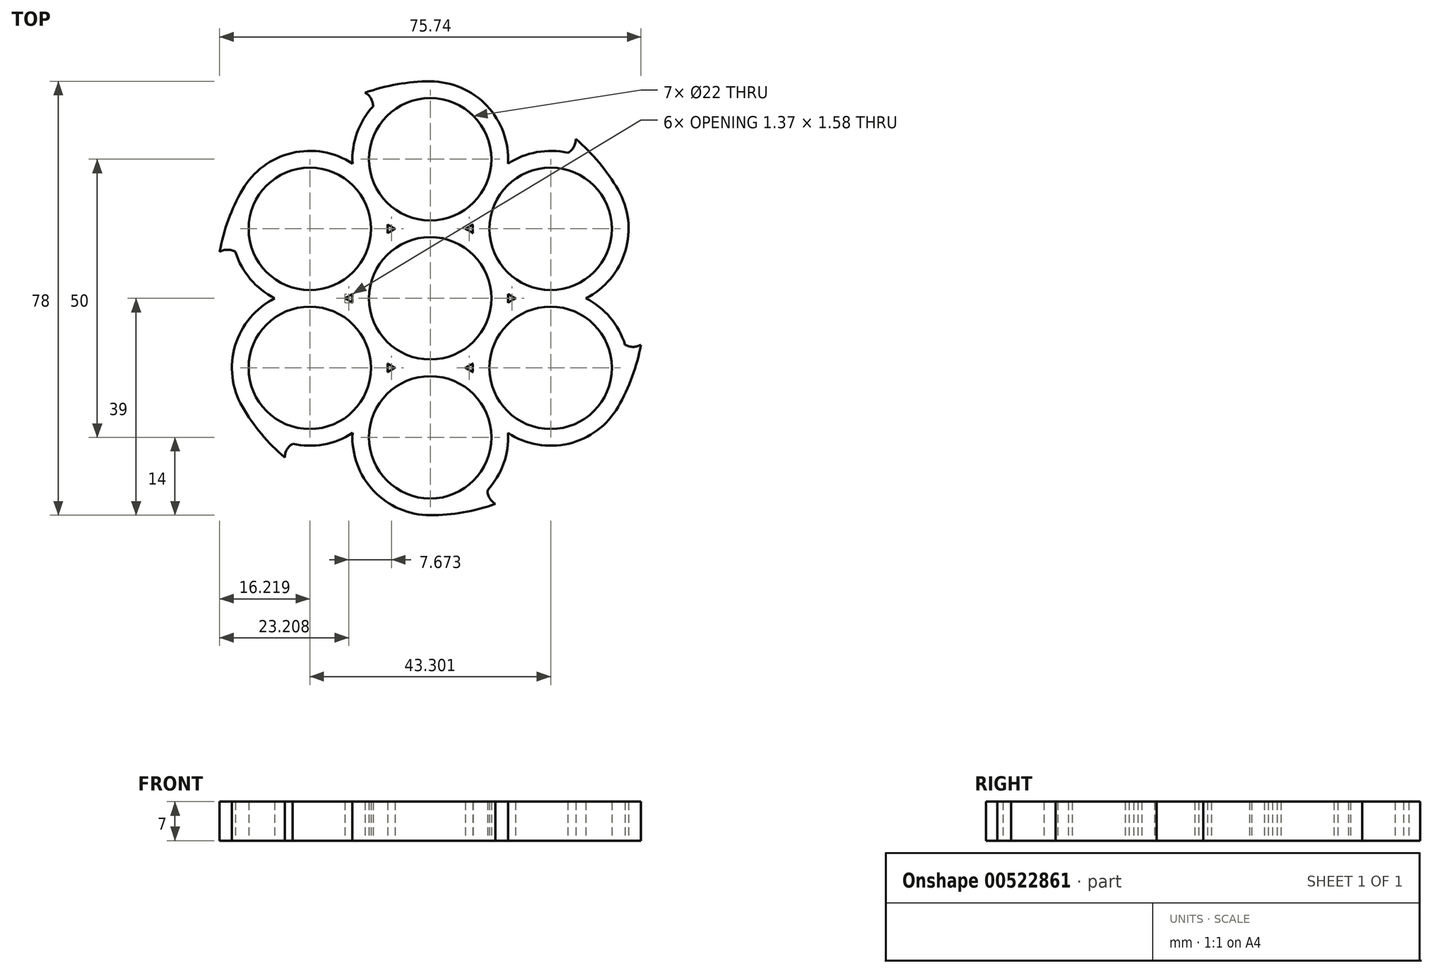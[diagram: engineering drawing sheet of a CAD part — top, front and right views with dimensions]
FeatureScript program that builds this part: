
annotation { "Feature Type Name" : "Feature", "Feature Type Description" : "" }
export const myFeature = defineFeature(function(context is Context, id is Id, definition is map)
    precondition{}
    {
        {
            var Q0;
            Q0=qCreatedBy(makeId("Top.planeOp"),FACE);
            var sketch = newSketch(context, id + "F0", { "sketchPlane" : qUnion([Q0])});
            skCircle(sketch, "E0", {"center": v(0, 0) * mm, "radius": 11 * mm});
            skArc(sketch, "E1", {"start": v(-13.98, 0.79) * mm, "mid": v(-14, 0) * mm, "end": v(-13.98, -0.79) * mm});
            skCircle(sketch, "E2", {"center": v(0, 25) * mm, "radius": 11 * mm});
            skArc(sketch, "E3", {"start": v(-7.67, 13.29) * mm, "mid": v(-7, 12.88) * mm, "end": v(-6.3, 12.5) * mm});
            skCircle(sketch, "E4.1.0", {"center": v(-21.65, 12.5) * mm, "radius": 11 * mm});
            skArc(sketch, "E4.1.1", {"start": v(-7.67, 11.71) * mm, "mid": v(-7.65, 12.5) * mm, "end": v(-7.67, 13.29) * mm});
            skCircle(sketch, "E4.2.0", {"center": v(-21.65, -12.5) * mm, "radius": 11 * mm});
            skArc(sketch, "E4.2.1", {"start": v(-7.67, -13.29) * mm, "mid": v(-7.65, -12.5) * mm, "end": v(-7.67, -11.71) * mm});
            skCircle(sketch, "E4.3.0", {"center": v(0, -25) * mm, "radius": 11 * mm});
            skArc(sketch, "E4.3.1", {"start": v(7.67, -13.29) * mm, "mid": v(7, -12.88) * mm, "end": v(6.3, -12.5) * mm});
            skCircle(sketch, "E4.4.0", {"center": v(21.65, -12.5) * mm, "radius": 11 * mm});
            skArc(sketch, "E4.4.1", {"start": v(7.67, -11.71) * mm, "mid": v(7.65, -12.5) * mm, "end": v(7.67, -13.29) * mm});
            skCircle(sketch, "E4.5.0", {"center": v(21.65, 12.5) * mm, "radius": 11 * mm});
            skArc(sketch, "E4.5.1", {"start": v(7.67, 13.29) * mm, "mid": v(7.65, 12.5) * mm, "end": v(7.67, 11.71) * mm});
            skArc(sketch, "E5.trimOffspring", {"start": v(-13.98, 24.21) * mm, "mid": v(-33.77, 19.5) * mm, "end": v(-27.96, 0) * mm});
            skArc(sketch, "E6.trimOffspring", {"start": v(-6.3, 12.5) * mm, "mid": v(-7, 12.12) * mm, "end": v(-7.67, 11.71) * mm});
            skArc(sketch, "E7.trimOffspring", {"start": v(6.3, 12.5) * mm, "mid": v(7, 12.88) * mm, "end": v(7.67, 13.29) * mm});
            skArc(sketch, "E8.trimOffspring", {"start": v(7.67, 11.71) * mm, "mid": v(7, 12.12) * mm, "end": v(6.3, 12.5) * mm});
            skArc(sketch, "E9.trimOffspring", {"start": v(13.98, 24.21) * mm, "mid": v(0, 39) * mm, "end": v(-13.98, 24.21) * mm});
            skArc(sketch, "E10.trimOffspring", {"start": v(13.98, 0.79) * mm, "mid": v(14.65, 0.38) * mm, "end": v(15.35, 0) * mm});
            skArc(sketch, "E11.trimOffspring", {"start": v(13.98, -0.79) * mm, "mid": v(14, 0) * mm, "end": v(13.98, 0.79) * mm});
            skArc(sketch, "E12.trimOffspring", {"start": v(27.96, 0) * mm, "mid": v(33.77, 19.5) * mm, "end": v(13.98, 24.21) * mm});
            skArc(sketch, "E13.trimOffspring", {"start": v(15.35, 0) * mm, "mid": v(14.65, -0.38) * mm, "end": v(13.98, -0.79) * mm});
            skArc(sketch, "E14.trimOffspring", {"start": v(13.98, -24.21) * mm, "mid": v(33.77, -19.5) * mm, "end": v(27.96, 0) * mm});
            skArc(sketch, "E15.trimOffspring", {"start": v(-6.3, -12.5) * mm, "mid": v(-7, -12.88) * mm, "end": v(-7.67, -13.29) * mm});
            skArc(sketch, "E16.trimOffspring", {"start": v(6.3, -12.5) * mm, "mid": v(7, -12.12) * mm, "end": v(7.67, -11.71) * mm});
            skArc(sketch, "E17.trimOffspring", {"start": v(-13.98, -24.21) * mm, "mid": v(0, -39) * mm, "end": v(13.98, -24.21) * mm});
            skArc(sketch, "E18.trimOffspring", {"start": v(-13.98, -0.79) * mm, "mid": v(-14.65, -0.38) * mm, "end": v(-15.35, 0) * mm});
            skArc(sketch, "E19.trimOffspring", {"start": v(-7.67, -11.71) * mm, "mid": v(-7, -12.12) * mm, "end": v(-6.3, -12.5) * mm});
            skArc(sketch, "E20.trimOffspring", {"start": v(-15.35, 0) * mm, "mid": v(-14.65, 0.38) * mm, "end": v(-13.98, 0.79) * mm});
            skArc(sketch, "E21.trimOffspring", {"start": v(-27.96, 0) * mm, "mid": v(-33.77, -19.5) * mm, "end": v(-13.98, -24.21) * mm});
            skArc(sketch, "E22", {"start": v(0, 39) * mm, "mid": v(-5.94, 38.49) * mm, "end": v(-11.7, 36.97) * mm});
            skArc(sketch, "E23", {"start": v(-10.28, 34.5) * mm, "mid": v(-10.66, 35.93) * mm, "end": v(-11.7, 36.97) * mm});
            skArc(sketch, "E24.1.0", {"start": v(-33.77, 19.5) * mm, "mid": v(-36.3, 14.1) * mm, "end": v(-37.87, 8.34) * mm});
            skArc(sketch, "E24.1.1", {"start": v(-35.02, 8.35) * mm, "mid": v(-36.45, 8.73) * mm, "end": v(-37.87, 8.34) * mm});
            skArc(sketch, "E24.2.0", {"start": v(-33.77, -19.5) * mm, "mid": v(-30.36, -24.4) * mm, "end": v(-26.16, -28.62) * mm});
            skArc(sketch, "E24.2.1", {"start": v(-24.74, -26.16) * mm, "mid": v(-25.79, -27.2) * mm, "end": v(-26.16, -28.62) * mm});
            skArc(sketch, "E24.3.0", {"start": v(0, -39) * mm, "mid": v(5.94, -38.49) * mm, "end": v(11.7, -36.97) * mm});
            skArc(sketch, "E24.3.1", {"start": v(10.28, -34.5) * mm, "mid": v(10.66, -35.93) * mm, "end": v(11.7, -36.97) * mm});
            skArc(sketch, "E24.4.0", {"start": v(33.77, -19.5) * mm, "mid": v(36.3, -14.1) * mm, "end": v(37.87, -8.34) * mm});
            skArc(sketch, "E24.4.1", {"start": v(35.02, -8.35) * mm, "mid": v(36.45, -8.73) * mm, "end": v(37.87, -8.34) * mm});
            skArc(sketch, "E24.5.0", {"start": v(33.77, 19.5) * mm, "mid": v(30.36, 24.4) * mm, "end": v(26.16, 28.62) * mm});
            skArc(sketch, "E24.5.1", {"start": v(24.74, 26.16) * mm, "mid": v(25.79, 27.2) * mm, "end": v(26.16, 28.62) * mm});
            skSolve(sketch);
        }
        {
            var Q0;
            Q0=qSketchRegion(id+"F0",true);
            extrude(context, id + "F1", {"entities" : qUnion([Q0]), "depth" : 7 * mm, "offsetDistance" : 25 * mm});
        }
    });
